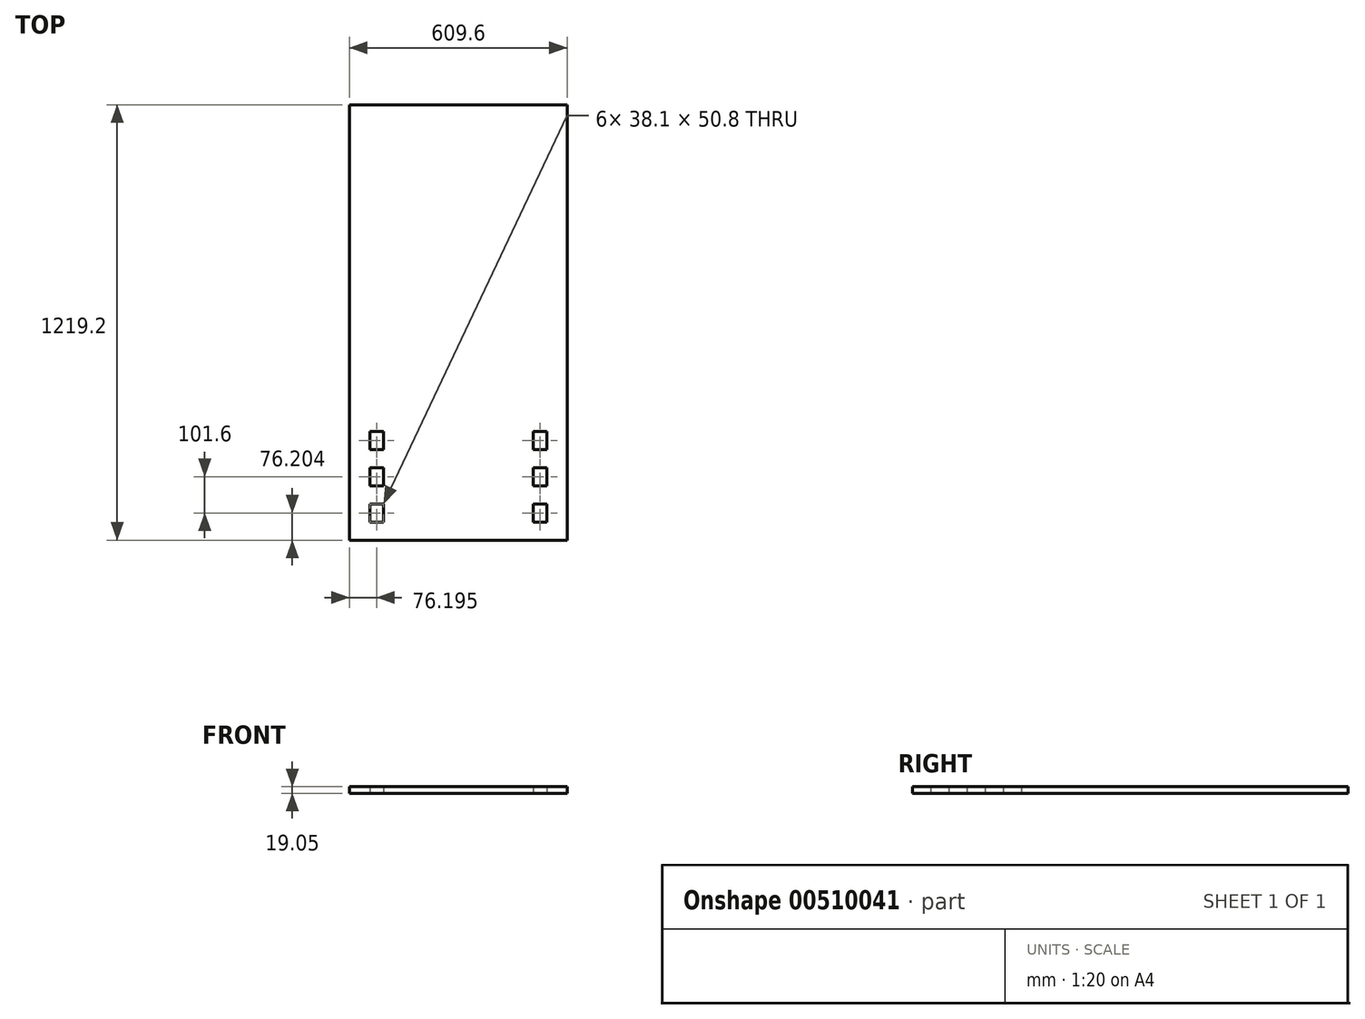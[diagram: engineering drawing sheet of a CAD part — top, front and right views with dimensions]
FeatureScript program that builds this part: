
annotation { "Feature Type Name" : "Feature", "Feature Type Description" : "" }
export const myFeature = defineFeature(function(context is Context, id is Id, definition is map)
    precondition{}
    {
        {
            var Q0;
            Q0=qCreatedBy(makeId("Top.planeOp"),FACE);
            var sketch = newSketch(context, id + "F0", { "sketchPlane" : qUnion([Q0])});
            skLineSegment(sketch, "E0", {"start": v(-228.55, -44.2) * mm, "end": v(381.05, -44.2) * mm});
            skLineSegment(sketch, "E1", {"start": v(-228.55, -44.2) * mm, "end": v(-228.55, 1175) * mm});
            skLineSegment(sketch, "E2", {"start": v(381.05, -44.2) * mm, "end": v(381.05, 1175) * mm});
            skLineSegment(sketch, "E3", {"start": v(381.05, 1175) * mm, "end": v(-228.55, 1175) * mm});
            skLineSegment(sketch, "E4.bottom", {"start": v(-152.4, 89.7) * mm, "end": v(-152.35, 89.7) * mm});
            skLineSegment(sketch, "E5.0", {"start": v(-228.52, 32) * mm, "end": v(381.08, 32) * mm, "construction": true});
            skPoint(sketch, "E6.middle", {"position": v(-152.32, 32) * mm});
            skLineSegment(sketch, "E7.MirrorCS", {"start": v(-152.35, -41.63) * mm, "end": v(-152.35, 1177.57) * mm, "construction": true});
            skLineSegment(sketch, "E8.left", {"start": v(285.8, 6.6) * mm, "end": v(285.8, 57.4) * mm});
            skLineSegment(sketch, "E8.right", {"start": v(323.9, 6.6) * mm, "end": v(323.9, 57.4) * mm});
            skLineSegment(sketch, "E9", {"start": v(285.8, 57.4) * mm, "end": v(323.9, 57.4) * mm});
            skLineSegment(sketch, "E10", {"start": v(285.8, 6.6) * mm, "end": v(323.9, 6.6) * mm});
            skLineSegment(sketch, "E11.direction1", {"start": v(285.8, 6.6) * mm, "end": v(311.2, 6.6) * mm, "construction": true});
            skLineSegment(sketch, "E12.0.1.0", {"start": v(323.9, 108.2) * mm, "end": v(323.9, 159) * mm});
            skLineSegment(sketch, "E12.0.1.1", {"start": v(285.8, 108.2) * mm, "end": v(285.8, 159) * mm});
            skLineSegment(sketch, "E12.0.1.2", {"start": v(285.8, 159) * mm, "end": v(323.9, 159) * mm});
            skLineSegment(sketch, "E12.0.1.3", {"start": v(285.8, 108.2) * mm, "end": v(323.9, 108.2) * mm});
            skLineSegment(sketch, "E12.0.1.4", {"start": v(285.8, 108.2) * mm, "end": v(311.2, 108.2) * mm, "construction": true});
            skLineSegment(sketch, "E12.0.2.0", {"start": v(323.9, 209.8) * mm, "end": v(323.9, 260.6) * mm});
            skLineSegment(sketch, "E12.0.2.1", {"start": v(285.8, 209.8) * mm, "end": v(285.8, 260.6) * mm});
            skLineSegment(sketch, "E12.0.2.2", {"start": v(285.8, 260.6) * mm, "end": v(323.9, 260.6) * mm});
            skLineSegment(sketch, "E12.0.2.3", {"start": v(285.8, 209.8) * mm, "end": v(323.9, 209.8) * mm});
            skLineSegment(sketch, "E12.0.2.4", {"start": v(285.8, 209.8) * mm, "end": v(311.2, 209.8) * mm, "construction": true});
            skLineSegment(sketch, "E13.MirrorCS", {"start": v(-133.3, 6.6) * mm, "end": v(-158.7, 6.6) * mm, "construction": true});
            skLineSegment(sketch, "E14.MirrorCS", {"start": v(-133.3, 6.6) * mm, "end": v(-171.4, 6.6) * mm});
            skLineSegment(sketch, "E15.MirrorCS", {"start": v(-133.3, 108.2) * mm, "end": v(-171.4, 108.2) * mm});
            skLineSegment(sketch, "E16.MirrorCS", {"start": v(-133.3, 209.8) * mm, "end": v(-171.4, 209.8) * mm});
            skLineSegment(sketch, "E17.MirrorCS", {"start": v(-133.3, 6.6) * mm, "end": v(-133.3, 57.4) * mm});
            skLineSegment(sketch, "E18.MirrorCS", {"start": v(-133.3, 209.8) * mm, "end": v(-158.7, 209.8) * mm, "construction": true});
            skLineSegment(sketch, "E19.MirrorCS", {"start": v(-133.3, 108.2) * mm, "end": v(-158.7, 108.2) * mm, "construction": true});
            skLineSegment(sketch, "E20.MirrorCS", {"start": v(-171.4, 6.6) * mm, "end": v(-171.4, 57.4) * mm});
            skLineSegment(sketch, "E21.MirrorCS", {"start": v(-133.3, 57.4) * mm, "end": v(-171.4, 57.4) * mm});
            skLineSegment(sketch, "E22.MirrorCS", {"start": v(-133.3, 159) * mm, "end": v(-171.4, 159) * mm});
            skLineSegment(sketch, "E23.MirrorCS", {"start": v(-171.4, 209.8) * mm, "end": v(-171.4, 260.6) * mm});
            skLineSegment(sketch, "E24.MirrorCS", {"start": v(-133.3, 108.2) * mm, "end": v(-133.3, 159) * mm});
            skLineSegment(sketch, "E25.MirrorCS", {"start": v(-133.3, 260.6) * mm, "end": v(-171.4, 260.6) * mm});
            skLineSegment(sketch, "E26.MirrorCS", {"start": v(-171.4, 108.2) * mm, "end": v(-171.4, 159) * mm});
            skLineSegment(sketch, "E27.MirrorCS", {"start": v(-133.3, 209.8) * mm, "end": v(-133.3, 260.6) * mm});
            skLineSegment(sketch, "E28", {"start": v(-133.3, 6.6) * mm, "end": v(285.8, 6.6) * mm, "construction": true});
            skSolve(sketch);
        }
        {
            var Q0;
            Q0 = qSketchRegion(id + "F0", true);
            extrude(context, id + "F1", {"entities" : qUnion([Q0]), "depth" : 19.05 * mm, "offsetDistance" : 25.4 * mm});
        }
    });
